# Revit family: Specialty_Equipment-Fiberglass_Planter-Planters_Unlimited-Baxter-Tapered Rectangular & Square-rev
name_source: partatom
category: Specialty Equipment
units: mm (PartAtom-declared; Revit-internal decimal feet)

## family parameters
Always vertical = Yes
Cut with Voids When Loaded = No
Enable Cutting in Views = No
Maintain Annotation Orientation = No
OmniClass Number = 23.40.05.21.17
OmniClass Title = Planters
Part Type = Normal
Room Calculation Point = No
Round Connector Dimension = Use Diameter
Shared = No
Work Plane-Based = No

## types (504) — shared parameters
Assembly Code = G2050600
CD_Finish = Plastic-Fiberglass-Carlsbad-Gloss-Black_Fox
CD_Microsite = https://www.caddetails.com
CD_Pad Size = 3"
CD_Pad Spacing = 5"
CD_Planter Lip = 1"
CD_Product Page URL = https://www.plantersunlimited.com
CD_Radius Baseplate = 6"
Default Elevation = 0"
Manufacturer = Planters Unlimited
Model = Baxter Tapered Series Planters
URL = https://www.plantersunlimited.com

## per-type parameters (varying)
| type | CD_Height | CD_Length | CD_Specification | CD_Width | Description | Type Comments |
| 30"L x 15"W x 18"H | 18" | 30" | https://www.plantersunlimited.com | 15" | Baxter Tapered Rectangular Planter | Tapered Rectangular Planter |
| 30"L x 15"W x 24"H | 24" | 30" | https://www.plantersunlimited.com | 15" | Baxter Tapered Rectangular Planter | Tapered Rectangular Planter |
| 30"L x 15"W x 30"H | 30" | 30" | https://www.plantersunlimited.com | 15" | Baxter Tapered Rectangular Planter | Tapered Rectangular Planter |
| 30"L x 15"W x 36"H | 36" | 30" | https://www.plantersunlimited.com | 15" | Baxter Tapered Rectangular Planter | Tapered Rectangular Planter |
| 30"L x 15"W x 42"H | 42" | 30" | https://www.plantersunlimited.com | 15" | Baxter Tapered Rectangular Planter | Tapered Rectangular Planter |
| 30"L x 15"W x 48"H | 48" | 30" | https://www.plantersunlimited.com | 15" | Baxter Tapered Rectangular Planter | Tapered Rectangular Planter |
| 30"L x 18"W x 18"H | 18" | 30" | https://www.plantersunlimited.com | 18" | Baxter Tapered Rectangular Planter | Tapered Rectangular Planter |
| 30"L x 18"W x 24"H | 24" | 30" | https://www.plantersunlimited.com | 18" | Baxter Tapered Rectangular Planter | Tapered Rectangular Planter |
| 30"L x 18"W x 30"H | 30" | 30" | https://www.plantersunlimited.com | 18" | Baxter Tapered Rectangular Planter | Tapered Rectangular Planter |
| 30"L x 18"W x 36"H | 36" | 30" | https://www.plantersunlimited.com | 18" | Baxter Tapered Rectangular Planter | Tapered Rectangular Planter |
| 30"L x 18"W x 42"H | 42" | 30" | https://www.plantersunlimited.com | 18" | Baxter Tapered Rectangular Planter | Tapered Rectangular Planter |
| 30"L x 18"W x 48"H | 48" | 30" | https://www.plantersunlimited.com | 18" | Baxter Tapered Rectangular Planter | Tapered Rectangular Planter |
| 30"L x 24"W x 18"H | 18" | 30" | https://www.plantersunlimited.com | 24" | Baxter Tapered Rectangular Planter | Tapered Rectangular Planter |
| 30"L x 24"W x 24"H | 24" | 30" | https://www.plantersunlimited.com | 24" | Baxter Tapered Rectangular Planter | Tapered Rectangular Planter |
| 30"L x 24"W x 30"H | 30" | 30" | https://www.plantersunlimited.com | 24" | Baxter Tapered Rectangular Planter | Tapered Rectangular Planter |
| 30"L x 24"W x 36"H | 36" | 30" | https://www.plantersunlimited.com | 24" | Baxter Tapered Rectangular Planter | Tapered Rectangular Planter |
| 30"L x 24"W x 42"H | 42" | 30" | https://www.plantersunlimited.com | 24" | Baxter Tapered Rectangular Planter | Tapered Rectangular Planter |
| 30"L x 24"W x 48"H | 48" | 30" | https://www.plantersunlimited.com | 24" | Baxter Tapered Rectangular Planter | Tapered Rectangular Planter |
| 30"L x 30"W x 18"H | 18" | 30" | https://www.plantersunlimited.com | 30" | Baxter Tapered Square Planter | Tapered Square Planter |
| 30"L x 30"W x 24"H | 24" | 30" | https://www.plantersunlimited.com | 30" | Baxter Tapered Square Planter | Tapered Square Planter |
| 30"L x 30"W x 30"H | 30" | 30" | https://www.plantersunlimited.com | 30" | Baxter Tapered Square Planter | Tapered Square Planter |
| 30"L x 30"W x 36"H | 36" | 30" |  | 30" | Baxter Tapered Square Planter | Tapered Square Planter |
| 30"L x 30"W x 42"H | 42" | 30" | https://www.plantersunlimited.com | 30" | Baxter Tapered Square Planter | Tapered Square Planter |
| 30"L x 30"W x 48"H | 48" | 30" | https://www.plantersunlimited.com | 30" | Baxter Tapered Square Planter | Tapered Square Planter |
| 30"L x 36"W x 18"H | 18" | 30" | https://www.plantersunlimited.com | 36" | Baxter Tapered Rectangular Planter | Tapered Rectangular Planter |
| 30"L x 36"W x 24"H | 24" | 30" | https://www.plantersunlimited.com | 36" | Baxter Tapered Rectangular Planter | Tapered Rectangular Planter |
| 30"L x 36"W x 30"H | 30" | 30" | https://www.plantersunlimited.com | 36" | Baxter Tapered Rectangular Planter | Tapered Rectangular Planter |
| 30"L x 36"W x 36"H | 36" | 30" | https://www.plantersunlimited.com | 36" | Baxter Tapered Rectangular Planter | Tapered Rectangular Planter |
| 30"L x 36"W x 42"H | 42" | 30" | https://www.plantersunlimited.com | 36" | Baxter Tapered Rectangular Planter | Tapered Rectangular Planter |
| 30"L x 36"W x 48"H | 48" | 30" | https://www.plantersunlimited.com | 36" | Baxter Tapered Rectangular Planter | Tapered Rectangular Planter |
| 30"L x 42"W x 18"H | 18" | 30" | https://www.plantersunlimited.com | 42" | Baxter Tapered Rectangular Planter | Tapered Rectangular Planter |
| 30"L x 42"W x 24"H | 24" | 30" | https://www.plantersunlimited.com | 42" | Baxter Tapered Rectangular Planter | Tapered Rectangular Planter |
| 30"L x 42"W x 30"H | 30" | 30" | https://www.plantersunlimited.com | 42" | Baxter Tapered Rectangular Planter | Tapered Rectangular Planter |
| 30"L x 42"W x 36"H | 36" | 30" | https://www.plantersunlimited.com | 42" | Baxter Tapered Rectangular Planter | Tapered Rectangular Planter |
| 30"L x 42"W x 42"H | 42" | 30" | https://www.plantersunlimited.com | 42" | Baxter Tapered Rectangular Planter | Tapered Rectangular Planter |
| 30"L x 42"W x 48"H | 48" | 30" | https://www.plantersunlimited.com | 42" | Baxter Tapered Rectangular Planter | Tapered Rectangular Planter |
| 36"L x 15"W x 18"H | 18" | 36" | https://www.plantersunlimited.com | 15" | Baxter Tapered Rectangular Planter | Tapered Rectangular Planter |
| 36"L x 15"W x 24"H | 24" | 36" | https://www.plantersunlimited.com | 15" | Baxter Tapered Rectangular Planter | Tapered Rectangular Planter |
| 36"L x 15"W x 30"H | 30" | 36" | https://www.plantersunlimited.com | 15" | Baxter Tapered Rectangular Planter | Tapered Rectangular Planter |
| 36"L x 15"W x 36"H | 36" | 36" | https://www.plantersunlimited.com | 15" | Baxter Tapered Rectangular Planter | Tapered Rectangular Planter |
| 36"L x 15"W x 42"H | 42" | 36" | https://www.plantersunlimited.com | 15" | Baxter Tapered Rectangular Planter | Tapered Rectangular Planter |
| 36"L x 15"W x 48"H | 48" | 36" | https://www.plantersunlimited.com | 15" | Baxter Tapered Rectangular Planter | Tapered Rectangular Planter |
| 36"L x 18"W x 18"H | 18" | 36" | https://www.plantersunlimited.com | 18" | Baxter Tapered Rectangular Planter | Tapered Rectangular Planter |
| 36"L x 18"W x 24"H | 24" | 36" | https://www.plantersunlimited.com | 18" | Baxter Tapered Rectangular Planter | Tapered Rectangular Planter |
| 36"L x 18"W x 30"H | 30" | 36" | https://www.plantersunlimited.com | 18" | Baxter Tapered Rectangular Planter | Tapered Rectangular Planter |
| 36"L x 18"W x 36"H | 36" | 36" | https://www.plantersunlimited.com | 18" | Baxter Tapered Rectangular Planter | Tapered Rectangular Planter |
| 36"L x 18"W x 42"H | 42" | 36" | https://www.plantersunlimited.com | 18" | Baxter Tapered Rectangular Planter | Tapered Rectangular Planter |
| 36"L x 18"W x 48"H | 48" | 36" | https://www.plantersunlimited.com | 18" | Baxter Tapered Rectangular Planter | Tapered Rectangular Planter |
| 36"L x 24"W x 18"H | 18" | 36" | https://www.plantersunlimited.com | 24" | Baxter Tapered Rectangular Planter | Tapered Rectangular Planter |
| 36"L x 24"W x 24"H | 24" | 36" | https://www.plantersunlimited.com | 24" | Baxter Tapered Rectangular Planter | Tapered Rectangular Planter |
| 36"L x 24"W x 30"H | 30" | 36" | https://www.plantersunlimited.com | 24" | Baxter Tapered Rectangular Planter | Tapered Rectangular Planter |
| 36"L x 24"W x 36"H | 36" | 36" | https://www.plantersunlimited.com | 24" | Baxter Tapered Rectangular Planter | Tapered Rectangular Planter |
| 36"L x 24"W x 42"H | 42" | 36" | https://www.plantersunlimited.com | 24" | Baxter Tapered Rectangular Planter | Tapered Rectangular Planter |
| 36"L x 24"W x 48"H | 48" | 36" | https://www.plantersunlimited.com | 24" | Baxter Tapered Rectangular Planter | Tapered Rectangular Planter |
| 36"L x 30"W x 18"H | 18" | 36" | https://www.plantersunlimited.com | 30" | Baxter Tapered Rectangular Planter | Tapered Rectangular Planter |
| 36"L x 30"W x 24"H | 24" | 36" | https://www.plantersunlimited.com | 30" | Baxter Tapered Rectangular Planter | Tapered Rectangular Planter |
| 36"L x 30"W x 30"H | 30" | 36" | https://www.plantersunlimited.com | 30" | Baxter Tapered Rectangular Planter | Tapered Rectangular Planter |
| 36"L x 30"W x 36"H | 36" | 36" | https://www.plantersunlimited.com | 30" | Baxter Tapered Rectangular Planter | Tapered Rectangular Planter |
| 36"L x 30"W x 42"H | 42" | 36" | https://www.plantersunlimited.com | 30" | Baxter Tapered Rectangular Planter | Tapered Rectangular Planter |
| 36"L x 30"W x 48"H | 48" | 36" | https://www.plantersunlimited.com | 30" | Baxter Tapered Rectangular Planter | Tapered Rectangular Planter |
| 36"L x 36"W x 18"H | 18" | 36" | https://www.plantersunlimited.com | 36" | Baxter Tapered Square Planter | Tapered Square Planter |
| 36"L x 36"W x 24"H | 24" | 36" | https://www.plantersunlimited.com | 36" | Baxter Tapered Square Planter | Tapered Square Planter |
| 36"L x 36"W x 30"H | 30" | 36" | https://www.plantersunlimited.com | 36" | Baxter Tapered Square Planter | Tapered Square Planter |
| 36"L x 36"W x 36"H | 36" | 36" | https://www.plantersunlimited.com | 36" | Baxter Tapered Square Planter | Tapered Square Planter |
| 36"L x 36"W x 42"H | 42" | 36" | https://www.plantersunlimited.com | 36" | Baxter Tapered Square Planter | Tapered Square Planter |
| 36"L x 36"W x 48"H | 48" | 36" | https://www.plantersunlimited.com | 36" | Baxter Tapered Square Planter | Tapered Square Planter |
| 36"L x 42"W x 18"H | 18" | 36" | https://www.plantersunlimited.com | 42" | Baxter Tapered Rectangular Planter | Tapered Rectangular Planter |
| 36"L x 42"W x 24"H | 24" | 36" | https://www.plantersunlimited.com | 42" | Baxter Tapered Rectangular Planter | Tapered Rectangular Planter |
| 36"L x 42"W x 30"H | 30" | 36" | https://www.plantersunlimited.com | 42" | Baxter Tapered Rectangular Planter | Tapered Rectangular Planter |
| 36"L x 42"W x 36"H | 36" | 36" | https://www.plantersunlimited.com | 42" | Baxter Tapered Rectangular Planter | Tapered Rectangular Planter |
| 36"L x 42"W x 42"H | 42" | 36" | https://www.plantersunlimited.com | 42" | Baxter Tapered Rectangular Planter | Tapered Rectangular Planter |
| 36"L x 42"W x 48"H | 48" | 36" | https://www.plantersunlimited.com | 42" | Baxter Tapered Rectangular Planter | Tapered Rectangular Planter |
| 42"L x 15"W x 18"H | 18" | 42" | https://www.plantersunlimited.com | 15" | Baxter Tapered Rectangular Planter | Tapered Rectangular Planter |
| 42"L x 15"W x 24"H | 24" | 42" | https://www.plantersunlimited.com | 15" | Baxter Tapered Rectangular Planter | Tapered Rectangular Planter |
| 42"L x 15"W x 30"H | 30" | 42" | https://www.plantersunlimited.com | 15" | Baxter Tapered Rectangular Planter | Tapered Rectangular Planter |
| 42"L x 15"W x 36"H | 36" | 42" | https://www.plantersunlimited.com | 15" | Baxter Tapered Rectangular Planter | Tapered Rectangular Planter |
| 42"L x 15"W x 42"H | 42" | 42" | https://www.plantersunlimited.com | 15" | Baxter Tapered Rectangular Planter | Tapered Rectangular Planter |
| 42"L x 15"W x 48"H | 48" | 42" | https://www.plantersunlimited.com | 15" | Baxter Tapered Rectangular Planter | Tapered Rectangular Planter |
| 42"L x 18"W x 18"H | 18" | 42" | https://www.plantersunlimited.com | 18" | Baxter Tapered Rectangular Planter | Tapered Rectangular Planter |
| 42"L x 18"W x 24"H | 24" | 42" | https://www.plantersunlimited.com | 18" | Baxter Tapered Rectangular Planter | Tapered Rectangular Planter |
| 42"L x 18"W x 30"H | 30" | 42" | https://www.plantersunlimited.com | 18" | Baxter Tapered Rectangular Planter | Tapered Rectangular Planter |
| 42"L x 18"W x 36"H | 36" | 42" | https://www.plantersunlimited.com | 18" | Baxter Tapered Rectangular Planter | Tapered Rectangular Planter |
| 42"L x 18"W x 42"H | 42" | 42" | https://www.plantersunlimited.com | 18" | Baxter Tapered Rectangular Planter | Tapered Rectangular Planter |
| 42"L x 18"W x 48"H | 48" | 42" | https://www.plantersunlimited.com | 18" | Baxter Tapered Rectangular Planter | Tapered Rectangular Planter |
| 42"L x 24"W x 18"H | 18" | 42" | https://www.plantersunlimited.com | 24" | Baxter Tapered Rectangular Planter | Tapered Rectangular Planter |
| 42"L x 24"W x 24"H | 24" | 42" | https://www.plantersunlimited.com | 24" | Baxter Tapered Rectangular Planter | Tapered Rectangular Planter |
| 42"L x 24"W x 30"H | 30" | 42" | https://www.plantersunlimited.com | 24" | Baxter Tapered Rectangular Planter | Tapered Rectangular Planter |
| 42"L x 24"W x 36"H | 36" | 42" | https://www.plantersunlimited.com | 24" | Baxter Tapered Rectangular Planter | Tapered Rectangular Planter |
| 42"L x 24"W x 42"H | 42" | 42" | https://www.plantersunlimited.com | 24" | Baxter Tapered Rectangular Planter | Tapered Rectangular Planter |
| 42"L x 24"W x 48"H | 48" | 42" | https://www.plantersunlimited.com | 24" | Baxter Tapered Rectangular Planter | Tapered Rectangular Planter |
| 42"L x 30"W x 18"H | 18" | 42" | https://www.plantersunlimited.com | 30" | Baxter Tapered Rectangular Planter | Tapered Rectangular Planter |
| 42"L x 30"W x 24"H | 24" | 42" | https://www.plantersunlimited.com | 30" | Baxter Tapered Rectangular Planter | Tapered Rectangular Planter |
| 42"L x 30"W x 30"H | 30" | 42" | https://www.plantersunlimited.com | 30" | Baxter Tapered Rectangular Planter | Tapered Rectangular Planter |
| 42"L x 30"W x 36"H | 36" | 42" | https://www.plantersunlimited.com | 30" | Baxter Tapered Rectangular Planter | Tapered Rectangular Planter |
| 42"L x 30"W x 42"H | 42" | 42" | https://www.plantersunlimited.com | 30" | Baxter Tapered Rectangular Planter | Tapered Rectangular Planter |
| 42"L x 30"W x 48"H | 48" | 42" | https://www.plantersunlimited.com | 30" | Baxter Tapered Rectangular Planter | Tapered Rectangular Planter |
| 42"L x 36"W x 18"H | 18" | 42" | https://www.plantersunlimited.com | 36" | Baxter Tapered Rectangular Planter | Tapered Rectangular Planter |
| 42"L x 36"W x 24"H | 24" | 42" | https://www.plantersunlimited.com | 36" | Baxter Tapered Rectangular Planter | Tapered Rectangular Planter |
| 42"L x 36"W x 30"H | 30" | 42" | https://www.plantersunlimited.com | 36" | Baxter Tapered Rectangular Planter | Tapered Rectangular Planter |
| 42"L x 36"W x 36"H | 36" | 42" | https://www.plantersunlimited.com | 36" | Baxter Tapered Rectangular Planter | Tapered Rectangular Planter |
| 42"L x 36"W x 42"H | 42" | 42" | https://www.plantersunlimited.com | 36" | Baxter Tapered Rectangular Planter | Tapered Rectangular Planter |
| 42"L x 36"W x 48"H | 48" | 42" | https://www.plantersunlimited.com | 36" | Baxter Tapered Rectangular Planter | Tapered Rectangular Planter |
| 42"L x 42"W x 18"H | 18" | 42" | https://www.plantersunlimited.com | 42" | Baxter Tapered Square Planter | Tapered Square Planter |
| 42"L x 42"W x 24"H | 24" | 42" | https://www.plantersunlimited.com | 42" | Baxter Tapered Square Planter | Tapered Square Planter |
| 42"L x 42"W x 30"H | 30" | 42" | https://www.plantersunlimited.com | 42" | Baxter Tapered Square Planter | Tapered Square Planter |
| 42"L x 42"W x 36"H | 36" | 42" | https://www.plantersunlimited.com | 42" | Baxter Tapered Square Planter | Tapered Square Planter |
| 42"L x 42"W x 42"H | 42" | 42" | https://www.plantersunlimited.com | 42" | Baxter Tapered Square Planter | Tapered Square Planter |
| 42"L x 42"W x 48"H | 48" | 42" | https://www.plantersunlimited.com | 42" | Baxter Tapered Square Planter | Tapered Square Planter |
| 48"L x 15"W x 18"H | 18" | 48" | https://www.plantersunlimited.com | 15" | Baxter Tapered Rectangular Planter | Tapered Rectangular Planter |
| 48"L x 15"W x 24"H | 24" | 48" | https://www.plantersunlimited.com | 15" | Baxter Tapered Rectangular Planter | Tapered Rectangular Planter |
| 48"L x 15"W x 30"H | 30" | 48" | https://www.plantersunlimited.com | 15" | Baxter Tapered Rectangular Planter | Tapered Rectangular Planter |
| 48"L x 15"W x 36"H | 36" | 48" | https://www.plantersunlimited.com | 15" | Baxter Tapered Rectangular Planter | Tapered Rectangular Planter |
| 48"L x 15"W x 42"H | 42" | 48" | https://www.plantersunlimited.com | 15" | Baxter Tapered Rectangular Planter | Tapered Rectangular Planter |
| 48"L x 15"W x 48"H | 48" | 48" | https://www.plantersunlimited.com | 15" | Baxter Tapered Rectangular Planter | Tapered Rectangular Planter |
| 48"L x 18"W x 18"H | 18" | 48" | https://www.plantersunlimited.com | 18" | Baxter Tapered Rectangular Planter | Tapered Rectangular Planter |
| 48"L x 18"W x 24"H | 24" | 48" | https://www.plantersunlimited.com | 18" | Baxter Tapered Rectangular Planter | Tapered Rectangular Planter |
| 48"L x 18"W x 30"H | 30" | 48" | https://www.plantersunlimited.com | 18" | Baxter Tapered Rectangular Planter | Tapered Rectangular Planter |
| 48"L x 18"W x 36"H | 36" | 48" | https://www.plantersunlimited.com | 18" | Baxter Tapered Rectangular Planter | Tapered Rectangular Planter |
| 48"L x 18"W x 42"H | 42" | 48" | https://www.plantersunlimited.com | 18" | Baxter Tapered Rectangular Planter | Tapered Rectangular Planter |
| 48"L x 18"W x 48"H | 48" | 48" | https://www.plantersunlimited.com | 18" | Baxter Tapered Rectangular Planter | Tapered Rectangular Planter |
| 48"L x 24"W x 18"H | 18" | 48" | https://www.plantersunlimited.com | 24" | Baxter Tapered Rectangular Planter | Tapered Rectangular Planter |
| 48"L x 24"W x 24"H | 24" | 48" | https://www.plantersunlimited.com | 24" | Baxter Tapered Rectangular Planter | Tapered Rectangular Planter |
| 48"L x 24"W x 30"H | 30" | 48" | https://www.plantersunlimited.com | 24" | Baxter Tapered Rectangular Planter | Tapered Rectangular Planter |
| 48"L x 24"W x 36"H | 36" | 48" | https://www.plantersunlimited.com | 24" | Baxter Tapered Rectangular Planter | Tapered Rectangular Planter |
| 48"L x 24"W x 42"H | 42" | 48" | https://www.plantersunlimited.com | 24" | Baxter Tapered Rectangular Planter | Tapered Rectangular Planter |
| 48"L x 24"W x 48"H | 48" | 48" | https://www.plantersunlimited.com | 24" | Baxter Tapered Rectangular Planter | Tapered Rectangular Planter |
| 48"L x 30"W x 18"H | 18" | 48" | https://www.plantersunlimited.com | 30" | Baxter Tapered Rectangular Planter | Tapered Rectangular Planter |
| 48"L x 30"W x 24"H | 24" | 48" | https://www.plantersunlimited.com | 30" | Baxter Tapered Rectangular Planter | Tapered Rectangular Planter |
| 48"L x 30"W x 30"H | 30" | 48" | https://www.plantersunlimited.com | 30" | Baxter Tapered Rectangular Planter | Tapered Rectangular Planter |
| 48"L x 30"W x 36"H | 36" | 48" | https://www.plantersunlimited.com | 30" | Baxter Tapered Rectangular Planter | Tapered Rectangular Planter |
| 48"L x 30"W x 42"H | 42" | 48" | https://www.plantersunlimited.com | 30" | Baxter Tapered Rectangular Planter | Tapered Rectangular Planter |
| 48"L x 30"W x 48"H | 48" | 48" | https://www.plantersunlimited.com | 30" | Baxter Tapered Rectangular Planter | Tapered Rectangular Planter |
| 48"L x 36"W x 18"H | 18" | 48" | https://www.plantersunlimited.com | 36" | Baxter Tapered Rectangular Planter | Tapered Rectangular Planter |
| 48"L x 36"W x 24"H | 24" | 48" | https://www.plantersunlimited.com | 36" | Baxter Tapered Rectangular Planter | Tapered Rectangular Planter |
| 48"L x 36"W x 30"H | 30" | 48" | https://www.plantersunlimited.com | 36" | Baxter Tapered Rectangular Planter | Tapered Rectangular Planter |
| 48"L x 36"W x 36"H | 36" | 48" | https://www.plantersunlimited.com | 36" | Baxter Tapered Rectangular Planter | Tapered Rectangular Planter |
| 48"L x 36"W x 42"H | 42" | 48" | https://www.plantersunlimited.com | 36" | Baxter Tapered Rectangular Planter | Tapered Rectangular Planter |
| 48"L x 36"W x 48"H | 48" | 48" | https://www.plantersunlimited.com | 36" | Baxter Tapered Rectangular Planter | Tapered Rectangular Planter |
| 48"L x 42"W x 18"H | 18" | 48" | https://www.plantersunlimited.com | 42" | Baxter Tapered Rectangular Planter | Tapered Rectangular Planter |
| 48"L x 42"W x 24"H | 24" | 48" | https://www.plantersunlimited.com | 42" | Baxter Tapered Rectangular Planter | Tapered Rectangular Planter |
| 48"L x 42"W x 30"H | 30" | 48" | https://www.plantersunlimited.com | 42" | Baxter Tapered Rectangular Planter | Tapered Rectangular Planter |
| 48"L x 42"W x 36"H | 36" | 48" | https://www.plantersunlimited.com | 42" | Baxter Tapered Rectangular Planter | Tapered Rectangular Planter |
| 48"L x 42"W x 42"H | 42" | 48" | https://www.plantersunlimited.com | 42" | Baxter Tapered Rectangular Planter | Tapered Rectangular Planter |
| 48"L x 42"W x 48"H | 48" | 48" | https://www.plantersunlimited.com | 42" | Baxter Tapered Rectangular Planter | Tapered Rectangular Planter |
| 54"L x 15"W x 18"H | 18" | 54" | https://www.plantersunlimited.com | 15" | Baxter Tapered Rectangular Planter | Tapered Rectangular Planter |
| 54"L x 15"W x 24"H | 24" | 54" | https://www.plantersunlimited.com | 15" | Baxter Tapered Rectangular Planter | Tapered Rectangular Planter |
| 54"L x 15"W x 30"H | 30" | 54" | https://www.plantersunlimited.com | 15" | Baxter Tapered Rectangular Planter | Tapered Rectangular Planter |
| 54"L x 15"W x 36"H | 36" | 54" | https://www.plantersunlimited.com | 15" | Baxter Tapered Rectangular Planter | Tapered Rectangular Planter |
| 54"L x 15"W x 42"H | 42" | 54" | https://www.plantersunlimited.com | 15" | Baxter Tapered Rectangular Planter | Tapered Rectangular Planter |
| 54"L x 15"W x 48"H | 48" | 54" | https://www.plantersunlimited.com | 15" | Baxter Tapered Rectangular Planter | Tapered Rectangular Planter |
| 54"L x 18"W x 18"H | 18" | 54" | https://www.plantersunlimited.com | 18" | Baxter Tapered Rectangular Planter | Tapered Rectangular Planter |
| 54"L x 18"W x 24"H | 24" | 54" | https://www.plantersunlimited.com | 18" | Baxter Tapered Rectangular Planter | Tapered Rectangular Planter |
| 54"L x 18"W x 30"H | 30" | 54" | https://www.plantersunlimited.com | 18" | Baxter Tapered Rectangular Planter | Tapered Rectangular Planter |
| 54"L x 18"W x 36"H | 36" | 54" | https://www.plantersunlimited.com | 18" | Baxter Tapered Rectangular Planter | Tapered Rectangular Planter |
| 54"L x 18"W x 42"H | 42" | 54" | https://www.plantersunlimited.com | 18" | Baxter Tapered Rectangular Planter | Tapered Rectangular Planter |
| 54"L x 18"W x 48"H | 48" | 54" | https://www.plantersunlimited.com | 18" | Baxter Tapered Rectangular Planter | Tapered Rectangular Planter |
| 54"L x 24"W x 18"H | 18" | 54" | https://www.plantersunlimited.com | 24" | Baxter Tapered Rectangular Planter | Tapered Rectangular Planter |
| 54"L x 24"W x 24"H | 24" | 54" | https://www.plantersunlimited.com | 24" | Baxter Tapered Rectangular Planter | Tapered Rectangular Planter |
| 54"L x 24"W x 30"H | 30" | 54" | https://www.plantersunlimited.com | 24" | Baxter Tapered Rectangular Planter | Tapered Rectangular Planter |
| 54"L x 24"W x 36"H | 36" | 54" | https://www.plantersunlimited.com | 24" | Baxter Tapered Rectangular Planter | Tapered Rectangular Planter |
| 54"L x 24"W x 42"H | 42" | 54" | https://www.plantersunlimited.com | 24" | Baxter Tapered Rectangular Planter | Tapered Rectangular Planter |
| 54"L x 24"W x 48"H | 48" | 54" | https://www.plantersunlimited.com | 24" | Baxter Tapered Rectangular Planter | Tapered Rectangular Planter |
| 54"L x 30"W x 18"H | 18" | 54" | https://www.plantersunlimited.com | 30" | Baxter Tapered Rectangular Planter | Tapered Rectangular Planter |
| 54"L x 30"W x 24"H | 24" | 54" | https://www.plantersunlimited.com | 30" | Baxter Tapered Rectangular Planter | Tapered Rectangular Planter |
| 54"L x 30"W x 30"H | 30" | 54" | https://www.plantersunlimited.com | 30" | Baxter Tapered Rectangular Planter | Tapered Rectangular Planter |
| 54"L x 30"W x 36"H | 36" | 54" | https://www.plantersunlimited.com | 30" | Baxter Tapered Rectangular Planter | Tapered Rectangular Planter |
| 54"L x 30"W x 42"H | 42" | 54" | https://www.plantersunlimited.com | 30" | Baxter Tapered Rectangular Planter | Tapered Rectangular Planter |
| 54"L x 30"W x 48"H | 48" | 54" | https://www.plantersunlimited.com | 30" | Baxter Tapered Rectangular Planter | Tapered Rectangular Planter |
| 54"L x 36"W x 18"H | 18" | 54" | https://www.plantersunlimited.com | 36" | Baxter Tapered Rectangular Planter | Tapered Rectangular Planter |
| 54"L x 36"W x 24"H | 24" | 54" | https://www.plantersunlimited.com | 36" | Baxter Tapered Rectangular Planter | Tapered Rectangular Planter |
| 54"L x 36"W x 30"H | 30" | 54" | https://www.plantersunlimited.com | 36" | Baxter Tapered Rectangular Planter | Tapered Rectangular Planter |
| 54"L x 36"W x 36"H | 36" | 54" | https://www.plantersunlimited.com | 36" | Baxter Tapered Rectangular Planter | Tapered Rectangular Planter |
| 54"L x 36"W x 42"H | 42" | 54" | https://www.plantersunlimited.com | 36" | Baxter Tapered Rectangular Planter | Tapered Rectangular Planter |
| 54"L x 36"W x 48"H | 48" | 54" | https://www.plantersunlimited.com | 36" | Baxter Tapered Rectangular Planter | Tapered Rectangular Planter |
| 54"L x 42"W x 18"H | 18" | 54" | https://www.plantersunlimited.com | 42" | Baxter Tapered Rectangular Planter | Tapered Rectangular Planter |
| 54"L x 42"W x 24"H | 24" | 54" | https://www.plantersunlimited.com | 42" | Baxter Tapered Rectangular Planter | Tapered Rectangular Planter |
| 54"L x 42"W x 30"H | 30" | 54" | https://www.plantersunlimited.com | 42" | Baxter Tapered Rectangular Planter | Tapered Rectangular Planter |
| 54"L x 42"W x 36"H | 36" | 54" | https://www.plantersunlimited.com | 42" | Baxter Tapered Rectangular Planter | Tapered Rectangular Planter |
| 54"L x 42"W x 42"H | 42" | 54" | https://www.plantersunlimited.com | 42" | Baxter Tapered Rectangular Planter | Tapered Rectangular Planter |
| 54"L x 42"W x 48"H | 48" | 54" | https://www.plantersunlimited.com | 42" | Baxter Tapered Rectangular Planter | Tapered Rectangular Planter |
| 60"L x 15"W x 18"H | 18" | 60" | https://www.plantersunlimited.com | 15" | Baxter Tapered Rectangular Planter | Tapered Rectangular Planter |
| 60"L x 15"W x 24"H | 24" | 60" | https://www.plantersunlimited.com | 15" | Baxter Tapered Rectangular Planter | Tapered Rectangular Planter |
| 60"L x 15"W x 30"H | 30" | 60" | https://www.plantersunlimited.com | 15" | Baxter Tapered Rectangular Planter | Tapered Rectangular Planter |
| 60"L x 15"W x 36"H | 36" | 60" | https://www.plantersunlimited.com | 15" | Baxter Tapered Rectangular Planter | Tapered Rectangular Planter |
| 60"L x 15"W x 42"H | 42" | 60" | https://www.plantersunlimited.com | 15" | Baxter Tapered Rectangular Planter | Tapered Rectangular Planter |
| 60"L x 15"W x 48"H | 48" | 60" | https://www.plantersunlimited.com | 15" | Baxter Tapered Rectangular Planter | Tapered Rectangular Planter |
| 60"L x 18"W x 18"H | 18" | 60" | https://www.plantersunlimited.com | 18" | Baxter Tapered Rectangular Planter | Tapered Rectangular Planter |
| 60"L x 18"W x 24"H | 24" | 60" | https://www.plantersunlimited.com | 18" | Baxter Tapered Rectangular Planter | Tapered Rectangular Planter |
| 60"L x 18"W x 30"H | 30" | 60" | https://www.plantersunlimited.com | 18" | Baxter Tapered Rectangular Planter | Tapered Rectangular Planter |
| 60"L x 18"W x 36"H | 36" | 60" | https://www.plantersunlimited.com | 18" | Baxter Tapered Rectangular Planter | Tapered Rectangular Planter |
| 60"L x 18"W x 42"H | 42" | 60" | https://www.plantersunlimited.com | 18" | Baxter Tapered Rectangular Planter | Tapered Rectangular Planter |
| 60"L x 18"W x 48"H | 48" | 60" | https://www.plantersunlimited.com | 18" | Baxter Tapered Rectangular Planter | Tapered Rectangular Planter |
| 60"L x 24"W x 18"H | 18" | 60" | https://www.plantersunlimited.com | 24" | Baxter Tapered Rectangular Planter | Tapered Rectangular Planter |
| 60"L x 24"W x 24"H | 24" | 60" | https://www.plantersunlimited.com | 24" | Baxter Tapered Rectangular Planter | Tapered Rectangular Planter |
| 60"L x 24"W x 30"H | 30" | 60" | https://www.plantersunlimited.com | 24" | Baxter Tapered Rectangular Planter | Tapered Rectangular Planter |
| 60"L x 24"W x 36"H | 36" | 60" | https://www.plantersunlimited.com | 24" | Baxter Tapered Rectangular Planter | Tapered Rectangular Planter |
| 60"L x 24"W x 42"H | 42" | 60" | https://www.plantersunlimited.com | 24" | Baxter Tapered Rectangular Planter | Tapered Rectangular Planter |
| 60"L x 24"W x 48"H | 48" | 60" | https://www.plantersunlimited.com | 24" | Baxter Tapered Rectangular Planter | Tapered Rectangular Planter |
| 60"L x 30"W x 18"H | 18" | 60" | https://www.plantersunlimited.com | 30" | Baxter Tapered Rectangular Planter | Tapered Rectangular Planter |
| 60"L x 30"W x 24"H | 24" | 60" | https://www.plantersunlimited.com | 30" | Baxter Tapered Rectangular Planter | Tapered Rectangular Planter |
| 60"L x 30"W x 30"H | 30" | 60" | https://www.plantersunlimited.com | 30" | Baxter Tapered Rectangular Planter | Tapered Rectangular Planter |
| 60"L x 30"W x 36"H | 36" | 60" | https://www.plantersunlimited.com | 30" | Baxter Tapered Rectangular Planter | Tapered Rectangular Planter |
| 60"L x 30"W x 42"H | 42" | 60" | https://www.plantersunlimited.com | 30" | Baxter Tapered Rectangular Planter | Tapered Rectangular Planter |
| 60"L x 30"W x 48"H | 48" | 60" | https://www.plantersunlimited.com | 30" | Baxter Tapered Rectangular Planter | Tapered Rectangular Planter |
| 60"L x 36"W x 18"H | 18" | 60" | https://www.plantersunlimited.com | 36" | Baxter Tapered Rectangular Planter | Tapered Rectangular Planter |
| 60"L x 36"W x 24"H | 24" | 60" | https://www.plantersunlimited.com | 36" | Baxter Tapered Rectangular Planter | Tapered Rectangular Planter |
| 60"L x 36"W x 30"H | 30" | 60" | https://www.plantersunlimited.com | 36" | Baxter Tapered Rectangular Planter | Tapered Rectangular Planter |
| 60"L x 36"W x 36"H | 36" | 60" | https://www.plantersunlimited.com | 36" | Baxter Tapered Rectangular Planter | Tapered Rectangular Planter |
| 60"L x 36"W x 42"H | 42" | 60" | https://www.plantersunlimited.com | 36" | Baxter Tapered Rectangular Planter | Tapered Rectangular Planter |
| 60"L x 36"W x 48"H | 48" | 60" | https://www.plantersunlimited.com | 36" | Baxter Tapered Rectangular Planter | Tapered Rectangular Planter |
| 60"L x 42"W x 18"H | 18" | 60" | https://www.plantersunlimited.com | 42" | Baxter Tapered Rectangular Planter | Tapered Rectangular Planter |
| 60"L x 42"W x 24"H | 24" | 60" | https://www.plantersunlimited.com | 42" | Baxter Tapered Rectangular Planter | Tapered Rectangular Planter |
| 60"L x 42"W x 30"H | 30" | 60" | https://www.plantersunlimited.com | 42" | Baxter Tapered Rectangular Planter | Tapered Rectangular Planter |
| 60"L x 42"W x 36"H | 36" | 60" | https://www.plantersunlimited.com | 42" | Baxter Tapered Rectangular Planter | Tapered Rectangular Planter |
| 60"L x 42"W x 42"H | 42" | 60" | https://www.plantersunlimited.com | 42" | Baxter Tapered Rectangular Planter | Tapered Rectangular Planter |
| 60"L x 42"W x 48"H | 48" | 60" | https://www.plantersunlimited.com | 42" | Baxter Tapered Rectangular Planter | Tapered Rectangular Planter |
| 66"L x 15"W x 18"H | 18" | 66" | https://www.plantersunlimited.com | 15" | Baxter Tapered Rectangular Planter | Tapered Rectangular Planter |
| 66"L x 15"W x 24"H | 24" | 66" | https://www.plantersunlimited.com | 15" | Baxter Tapered Rectangular Planter | Tapered Rectangular Planter |
| 66"L x 15"W x 30"H | 30" | 66" | https://www.plantersunlimited.com | 15" | Baxter Tapered Rectangular Planter | Tapered Rectangular Planter |
| 66"L x 15"W x 36"H | 36" | 66" | https://www.plantersunlimited.com | 15" | Baxter Tapered Rectangular Planter | Tapered Rectangular Planter |
| 66"L x 15"W x 42"H | 42" | 66" | https://www.plantersunlimited.com | 15" | Baxter Tapered Rectangular Planter | Tapered Rectangular Planter |
| 66"L x 15"W x 48"H | 48" | 66" | https://www.plantersunlimited.com | 15" | Baxter Tapered Rectangular Planter | Tapered Rectangular Planter |
| 66"L x 18"W x 18"H | 18" | 66" | https://www.plantersunlimited.com | 18" | Baxter Tapered Rectangular Planter | Tapered Rectangular Planter |
| 66"L x 18"W x 24"H | 24" | 66" | https://www.plantersunlimited.com | 18" | Baxter Tapered Rectangular Planter | Tapered Rectangular Planter |
| 66"L x 18"W x 30"H | 30" | 66" | https://www.plantersunlimited.com | 18" | Baxter Tapered Rectangular Planter | Tapered Rectangular Planter |
| 66"L x 18"W x 36"H | 36" | 66" | https://www.plantersunlimited.com | 18" | Baxter Tapered Rectangular Planter | Tapered Rectangular Planter |
| 66"L x 18"W x 42"H | 42" | 66" | https://www.plantersunlimited.com | 18" | Baxter Tapered Rectangular Planter | Tapered Rectangular Planter |
| 66"L x 18"W x 48"H | 48" | 66" | https://www.plantersunlimited.com | 18" | Baxter Tapered Rectangular Planter | Tapered Rectangular Planter |
| 66"L x 24"W x 18"H | 18" | 66" | https://www.plantersunlimited.com | 24" | Baxter Tapered Rectangular Planter | Tapered Rectangular Planter |
| 66"L x 24"W x 24"H | 24" | 66" | https://www.plantersunlimited.com | 24" | Baxter Tapered Rectangular Planter | Tapered Rectangular Planter |
| 66"L x 24"W x 30"H | 30" | 66" | https://www.plantersunlimited.com | 24" | Baxter Tapered Rectangular Planter | Tapered Rectangular Planter |
| 66"L x 24"W x 36"H | 36" | 66" | https://www.plantersunlimited.com | 24" | Baxter Tapered Rectangular Planter | Tapered Rectangular Planter |
| 66"L x 24"W x 42"H | 42" | 66" | https://www.plantersunlimited.com | 24" | Baxter Tapered Rectangular Planter | Tapered Rectangular Planter |
| 66"L x 24"W x 48"H | 48" | 66" | https://www.plantersunlimited.com | 24" | Baxter Tapered Rectangular Planter | Tapered Rectangular Planter |
| 66"L x 30"W x 18"H | 18" | 66" | https://www.plantersunlimited.com | 30" | Baxter Tapered Rectangular Planter | Tapered Rectangular Planter |
| 66"L x 30"W x 24"H | 24" | 66" | https://www.plantersunlimited.com | 30" | Baxter Tapered Rectangular Planter | Tapered Rectangular Planter |
| 66"L x 30"W x 30"H | 30" | 66" | https://www.plantersunlimited.com | 30" | Baxter Tapered Rectangular Planter | Tapered Rectangular Planter |
| 66"L x 30"W x 36"H | 36" | 66" | https://www.plantersunlimited.com | 30" | Baxter Tapered Rectangular Planter | Tapered Rectangular Planter |
| 66"L x 30"W x 42"H | 42" | 66" | https://www.plantersunlimited.com | 30" | Baxter Tapered Rectangular Planter | Tapered Rectangular Planter |
| 66"L x 30"W x 48"H | 48" | 66" | https://www.plantersunlimited.com | 30" | Baxter Tapered Rectangular Planter | Tapered Rectangular Planter |
| 66"L x 36"W x 18"H | 18" | 66" | https://www.plantersunlimited.com | 36" | Baxter Tapered Rectangular Planter | Tapered Rectangular Planter |
| 66"L x 36"W x 24"H | 24" | 66" | https://www.plantersunlimited.com | 36" | Baxter Tapered Rectangular Planter | Tapered Rectangular Planter |
| 66"L x 36"W x 30"H | 30" | 66" | https://www.plantersunlimited.com | 36" | Baxter Tapered Rectangular Planter | Tapered Rectangular Planter |
| 66"L x 36"W x 36"H | 36" | 66" | https://www.plantersunlimited.com | 36" | Baxter Tapered Rectangular Planter | Tapered Rectangular Planter |
| 66"L x 36"W x 42"H | 42" | 66" | https://www.plantersunlimited.com | 36" | Baxter Tapered Rectangular Planter | Tapered Rectangular Planter |
| 66"L x 36"W x 48"H | 48" | 66" | https://www.plantersunlimited.com | 36" | Baxter Tapered Rectangular Planter | Tapered Rectangular Planter |
| 66"L x 42"W x 18"H | 18" | 66" | https://www.plantersunlimited.com | 42" | Baxter Tapered Rectangular Planter | Tapered Rectangular Planter |
| 66"L x 42"W x 24"H | 24" | 66" | https://www.plantersunlimited.com | 42" | Baxter Tapered Rectangular Planter | Tapered Rectangular Planter |
| 66"L x 42"W x 30"H | 30" | 66" | https://www.plantersunlimited.com | 42" | Baxter Tapered Rectangular Planter | Tapered Rectangular Planter |
| 66"L x 42"W x 36"H | 36" | 66" | https://www.plantersunlimited.com | 42" | Baxter Tapered Rectangular Planter | Tapered Rectangular Planter |
| 66"L x 42"W x 42"H | 42" | 66" | https://www.plantersunlimited.com | 42" | Baxter Tapered Rectangular Planter | Tapered Rectangular Planter |
| 66"L x 42"W x 48"H | 48" | 66" | https://www.plantersunlimited.com | 42" | Baxter Tapered Rectangular Planter | Tapered Rectangular Planter |
| 72"L x 15"W x 18"H | 18" | 72" | https://www.plantersunlimited.com | 15" | Baxter Tapered Rectangular Planter | Tapered Rectangular Planter |
| 72"L x 15"W x 24"H | 24" | 72" | https://www.plantersunlimited.com | 15" | Baxter Tapered Rectangular Planter | Tapered Rectangular Planter |
| 72"L x 15"W x 30"H | 30" | 72" | https://www.plantersunlimited.com | 15" | Baxter Tapered Rectangular Planter | Tapered Rectangular Planter |
| 72"L x 15"W x 36"H | 36" | 72" | https://www.plantersunlimited.com | 15" | Baxter Tapered Rectangular Planter | Tapered Rectangular Planter |
| 72"L x 15"W x 42"H | 42" | 72" | https://www.plantersunlimited.com | 15" | Baxter Tapered Rectangular Planter | Tapered Rectangular Planter |
| 72"L x 15"W x 48"H | 48" | 72" | https://www.plantersunlimited.com | 15" | Baxter Tapered Rectangular Planter | Tapered Rectangular Planter |
| 72"L x 18"W x 18"H | 18" | 72" | https://www.plantersunlimited.com | 18" | Baxter Tapered Rectangular Planter | Tapered Rectangular Planter |
| 72"L x 18"W x 24"H | 24" | 72" | https://www.plantersunlimited.com | 18" | Baxter Tapered Rectangular Planter | Tapered Rectangular Planter |
| 72"L x 18"W x 30"H | 30" | 72" | https://www.plantersunlimited.com | 18" | Baxter Tapered Rectangular Planter | Tapered Rectangular Planter |
| 72"L x 18"W x 36"H | 36" | 72" | https://www.plantersunlimited.com | 18" | Baxter Tapered Rectangular Planter | Tapered Rectangular Planter |
| 72"L x 18"W x 42"H | 42" | 72" | https://www.plantersunlimited.com | 18" | Baxter Tapered Rectangular Planter | Tapered Rectangular Planter |
| 72"L x 18"W x 48"H | 48" | 72" | https://www.plantersunlimited.com | 18" | Baxter Tapered Rectangular Planter | Tapered Rectangular Planter |
| 72"L x 24"W x 18"H | 18" | 72" | https://www.plantersunlimited.com | 24" | Baxter Tapered Rectangular Planter | Tapered Rectangular Planter |
| 72"L x 24"W x 24"H | 24" | 72" | https://www.plantersunlimited.com | 24" | Baxter Tapered Rectangular Planter | Tapered Rectangular Planter |
| 72"L x 24"W x 30"H | 30" | 72" | https://www.plantersunlimited.com | 24" | Baxter Tapered Rectangular Planter | Tapered Rectangular Planter |
| 72"L x 24"W x 36"H | 36" | 72" | https://www.plantersunlimited.com | 24" | Baxter Tapered Rectangular Planter | Tapered Rectangular Planter |
| 72"L x 24"W x 42"H | 42" | 72" | https://www.plantersunlimited.com | 24" | Baxter Tapered Rectangular Planter | Tapered Rectangular Planter |
| 72"L x 24"W x 48"H | 48" | 72" | https://www.plantersunlimited.com | 24" | Baxter Tapered Rectangular Planter | Tapered Rectangular Planter |
| 72"L x 30"W x 18"H | 18" | 72" | https://www.plantersunlimited.com | 30" | Baxter Tapered Rectangular Planter | Tapered Rectangular Planter |
| 72"L x 30"W x 24"H | 24" | 72" | https://www.plantersunlimited.com | 30" | Baxter Tapered Rectangular Planter | Tapered Rectangular Planter |
| 72"L x 30"W x 30"H | 30" | 72" | https://www.plantersunlimited.com | 30" | Baxter Tapered Rectangular Planter | Tapered Rectangular Planter |
| 72"L x 30"W x 36"H | 36" | 72" | https://www.plantersunlimited.com | 30" | Baxter Tapered Rectangular Planter | Tapered Rectangular Planter |
| 72"L x 30"W x 42"H | 42" | 72" | https://www.plantersunlimited.com | 30" | Baxter Tapered Rectangular Planter | Tapered Rectangular Planter |
| 72"L x 30"W x 48"H | 48" | 72" | https://www.plantersunlimited.com | 30" | Baxter Tapered Rectangular Planter | Tapered Rectangular Planter |
| 72"L x 36"W x 18"H | 18" | 72" | https://www.plantersunlimited.com | 36" | Baxter Tapered Rectangular Planter | Tapered Rectangular Planter |
| 72"L x 36"W x 24"H | 24" | 72" | https://www.plantersunlimited.com | 36" | Baxter Tapered Rectangular Planter | Tapered Rectangular Planter |
| 72"L x 36"W x 30"H | 30" | 72" | https://www.plantersunlimited.com | 36" | Baxter Tapered Rectangular Planter | Tapered Rectangular Planter |
| 72"L x 36"W x 36"H | 36" | 72" | https://www.plantersunlimited.com | 36" | Baxter Tapered Rectangular Planter | Tapered Rectangular Planter |
| 72"L x 36"W x 42"H | 42" | 72" | https://www.plantersunlimited.com | 36" | Baxter Tapered Rectangular Planter | Tapered Rectangular Planter |
| 72"L x 36"W x 48"H | 48" | 72" | https://www.plantersunlimited.com | 36" | Baxter Tapered Rectangular Planter | Tapered Rectangular Planter |
| 72"L x 42"W x 18"H | 18" | 72" | https://www.plantersunlimited.com | 42" | Baxter Tapered Rectangular Planter | Tapered Rectangular Planter |
| 72"L x 42"W x 24"H | 24" | 72" | https://www.plantersunlimited.com | 42" | Baxter Tapered Rectangular Planter | Tapered Rectangular Planter |
| 72"L x 42"W x 30"H | 30" | 72" | https://www.plantersunlimited.com | 42" | Baxter Tapered Rectangular Planter | Tapered Rectangular Planter |
| 72"L x 42"W x 36"H | 36" | 72" | https://www.plantersunlimited.com | 42" | Baxter Tapered Rectangular Planter | Tapered Rectangular Planter |
| 72"L x 42"W x 42"H | 42" | 72" | https://www.plantersunlimited.com | 42" | Baxter Tapered Rectangular Planter | Tapered Rectangular Planter |
| 72"L x 42"W x 48"H | 48" | 72" | https://www.plantersunlimited.com | 42" | Baxter Tapered Rectangular Planter | Tapered Rectangular Planter |
| 78"L x 15"W x 18"H | 18" | 78" | https://www.plantersunlimited.com | 15" | Baxter Tapered Rectangular Planter | Tapered Rectangular Planter |
| 78"L x 15"W x 24"H | 24" | 78" | https://www.plantersunlimited.com | 15" | Baxter Tapered Rectangular Planter | Tapered Rectangular Planter |
| 78"L x 15"W x 30"H | 30" | 78" | https://www.plantersunlimited.com | 15" | Baxter Tapered Rectangular Planter | Tapered Rectangular Planter |
| 78"L x 15"W x 36"H | 36" | 78" | https://www.plantersunlimited.com | 15" | Baxter Tapered Rectangular Planter | Tapered Rectangular Planter |
| 78"L x 15"W x 42"H | 42" | 78" | https://www.plantersunlimited.com | 15" | Baxter Tapered Rectangular Planter | Tapered Rectangular Planter |
| 78"L x 15"W x 48"H | 48" | 78" | https://www.plantersunlimited.com | 15" | Baxter Tapered Rectangular Planter | Tapered Rectangular Planter |
| 78"L x 18"W x 18"H | 18" | 78" | https://www.plantersunlimited.com | 18" | Baxter Tapered Rectangular Planter | Tapered Rectangular Planter |
| 78"L x 18"W x 24"H | 24" | 78" | https://www.plantersunlimited.com | 18" | Baxter Tapered Rectangular Planter | Tapered Rectangular Planter |
| 78"L x 18"W x 30"H | 30" | 78" | https://www.plantersunlimited.com | 18" | Baxter Tapered Rectangular Planter | Tapered Rectangular Planter |
| 78"L x 18"W x 36"H | 36" | 78" | https://www.plantersunlimited.com | 18" | Baxter Tapered Rectangular Planter | Tapered Rectangular Planter |
| 78"L x 18"W x 42"H | 42" | 78" | https://www.plantersunlimited.com | 18" | Baxter Tapered Rectangular Planter | Tapered Rectangular Planter |
| 78"L x 18"W x 48"H | 48" | 78" | https://www.plantersunlimited.com | 18" | Baxter Tapered Rectangular Planter | Tapered Rectangular Planter |
| 78"L x 24"W x 18"H | 18" | 78" | https://www.plantersunlimited.com | 24" | Baxter Tapered Rectangular Planter | Tapered Rectangular Planter |
| 78"L x 24"W x 24"H | 24" | 78" | https://www.plantersunlimited.com | 24" | Baxter Tapered Rectangular Planter | Tapered Rectangular Planter |
| 78"L x 24"W x 30"H | 30" | 78" | https://www.plantersunlimited.com | 24" | Baxter Tapered Rectangular Planter | Tapered Rectangular Planter |
| 78"L x 24"W x 36"H | 36" | 78" | https://www.plantersunlimited.com | 24" | Baxter Tapered Rectangular Planter | Tapered Rectangular Planter |
| 78"L x 24"W x 42"H | 42" | 78" | https://www.plantersunlimited.com | 24" | Baxter Tapered Rectangular Planter | Tapered Rectangular Planter |
| 78"L x 24"W x 48"H | 48" | 78" | https://www.plantersunlimited.com | 24" | Baxter Tapered Rectangular Planter | Tapered Rectangular Planter |
| 78"L x 30"W x 18"H | 18" | 78" | https://www.plantersunlimited.com | 30" | Baxter Tapered Rectangular Planter | Tapered Rectangular Planter |
| 78"L x 30"W x 24"H | 24" | 78" | https://www.plantersunlimited.com | 30" | Baxter Tapered Rectangular Planter | Tapered Rectangular Planter |
| 78"L x 30"W x 30"H | 30" | 78" | https://www.plantersunlimited.com | 30" | Baxter Tapered Rectangular Planter | Tapered Rectangular Planter |
| 78"L x 30"W x 36"H | 36" | 78" | https://www.plantersunlimited.com | 30" | Baxter Tapered Rectangular Planter | Tapered Rectangular Planter |
| 78"L x 30"W x 42"H | 42" | 78" | https://www.plantersunlimited.com | 30" | Baxter Tapered Rectangular Planter | Tapered Rectangular Planter |
| 78"L x 30"W x 48"H | 48" | 78" | https://www.plantersunlimited.com | 30" | Baxter Tapered Rectangular Planter | Tapered Rectangular Planter |
| 78"L x 36"W x 18"H | 18" | 78" | https://www.plantersunlimited.com | 36" | Baxter Tapered Rectangular Planter | Tapered Rectangular Planter |
| 78"L x 36"W x 24"H | 24" | 78" | https://www.plantersunlimited.com | 36" | Baxter Tapered Rectangular Planter | Tapered Rectangular Planter |
| 78"L x 36"W x 30"H | 30" | 78" | https://www.plantersunlimited.com | 36" | Baxter Tapered Rectangular Planter | Tapered Rectangular Planter |
| 78"L x 36"W x 36"H | 36" | 78" | https://www.plantersunlimited.com | 36" | Baxter Tapered Rectangular Planter | Tapered Rectangular Planter |
| 78"L x 36"W x 42"H | 42" | 78" | https://www.plantersunlimited.com | 36" | Baxter Tapered Rectangular Planter | Tapered Rectangular Planter |
| 78"L x 36"W x 48"H | 48" | 78" | https://www.plantersunlimited.com | 36" | Baxter Tapered Rectangular Planter | Tapered Rectangular Planter |
| 78"L x 42"W x 18"H | 18" | 78" | https://www.plantersunlimited.com | 42" | Baxter Tapered Rectangular Planter | Tapered Rectangular Planter |
| 78"L x 42"W x 24"H | 24" | 78" | https://www.plantersunlimited.com | 42" | Baxter Tapered Rectangular Planter | Tapered Rectangular Planter |
| 78"L x 42"W x 30"H | 30" | 78" | https://www.plantersunlimited.com | 42" | Baxter Tapered Rectangular Planter | Tapered Rectangular Planter |
| 78"L x 42"W x 36"H | 36" | 78" | https://www.plantersunlimited.com | 42" | Baxter Tapered Rectangular Planter | Tapered Rectangular Planter |
| 78"L x 42"W x 42"H | 42" | 78" | https://www.plantersunlimited.com | 42" | Baxter Tapered Rectangular Planter | Tapered Rectangular Planter |
| 78"L x 42"W x 48"H | 48" | 78" | https://www.plantersunlimited.com | 42" | Baxter Tapered Rectangular Planter | Tapered Rectangular Planter |
| 84"L x 15"W x 18"H | 18" | 84" | https://www.plantersunlimited.com | 15" | Baxter Tapered Rectangular Planter | Tapered Rectangular Planter |
| 84"L x 15"W x 24"H | 24" | 84" | https://www.plantersunlimited.com | 15" | Baxter Tapered Rectangular Planter | Tapered Rectangular Planter |
| 84"L x 15"W x 30"H | 30" | 84" | https://www.plantersunlimited.com | 15" | Baxter Tapered Rectangular Planter | Tapered Rectangular Planter |
| 84"L x 15"W x 36"H | 36" | 84" | https://www.plantersunlimited.com | 15" | Baxter Tapered Rectangular Planter | Tapered Rectangular Planter |
| 84"L x 15"W x 42"H | 42" | 84" | https://www.plantersunlimited.com | 15" | Baxter Tapered Rectangular Planter | Tapered Rectangular Planter |
| 84"L x 15"W x 48"H | 48" | 84" | https://www.plantersunlimited.com | 15" | Baxter Tapered Rectangular Planter | Tapered Rectangular Planter |
| 84"L x 18"W x 18"H | 18" | 84" | https://www.plantersunlimited.com | 18" | Baxter Tapered Rectangular Planter | Tapered Rectangular Planter |
| 84"L x 18"W x 24"H | 24" | 84" | https://www.plantersunlimited.com | 18" | Baxter Tapered Rectangular Planter | Tapered Rectangular Planter |
| 84"L x 18"W x 30"H | 30" | 84" | https://www.plantersunlimited.com | 18" | Baxter Tapered Rectangular Planter | Tapered Rectangular Planter |
| 84"L x 18"W x 36"H | 36" | 84" | https://www.plantersunlimited.com | 18" | Baxter Tapered Rectangular Planter | Tapered Rectangular Planter |
| 84"L x 18"W x 42"H | 42" | 84" | https://www.plantersunlimited.com | 18" | Baxter Tapered Rectangular Planter | Tapered Rectangular Planter |
| 84"L x 18"W x 48"H | 48" | 84" | https://www.plantersunlimited.com | 18" | Baxter Tapered Rectangular Planter | Tapered Rectangular Planter |
| 84"L x 24"W x 18"H | 18" | 84" | https://www.plantersunlimited.com | 24" | Baxter Tapered Rectangular Planter | Tapered Rectangular Planter |
| 84"L x 24"W x 24"H | 24" | 84" | https://www.plantersunlimited.com | 24" | Baxter Tapered Rectangular Planter | Tapered Rectangular Planter |
| 84"L x 24"W x 30"H | 30" | 84" | https://www.plantersunlimited.com | 24" | Baxter Tapered Rectangular Planter | Tapered Rectangular Planter |
| 84"L x 24"W x 36"H | 36" | 84" | https://www.plantersunlimited.com | 24" | Baxter Tapered Rectangular Planter | Tapered Rectangular Planter |
| 84"L x 24"W x 42"H | 42" | 84" | https://www.plantersunlimited.com | 24" | Baxter Tapered Rectangular Planter | Tapered Rectangular Planter |
| 84"L x 24"W x 48"H | 48" | 84" | https://www.plantersunlimited.com | 24" | Baxter Tapered Rectangular Planter | Tapered Rectangular Planter |
| 84"L x 30"W x 18"H | 18" | 84" | https://www.plantersunlimited.com | 30" | Baxter Tapered Rectangular Planter | Tapered Rectangular Planter |
| 84"L x 30"W x 24"H | 24" | 84" | https://www.plantersunlimited.com | 30" | Baxter Tapered Rectangular Planter | Tapered Rectangular Planter |
| 84"L x 30"W x 30"H | 30" | 84" | https://www.plantersunlimited.com | 30" | Baxter Tapered Rectangular Planter | Tapered Rectangular Planter |
| 84"L x 30"W x 36"H | 36" | 84" | https://www.plantersunlimited.com | 30" | Baxter Tapered Rectangular Planter | Tapered Rectangular Planter |
| 84"L x 30"W x 42"H | 42" | 84" | https://www.plantersunlimited.com | 30" | Baxter Tapered Rectangular Planter | Tapered Rectangular Planter |
| 84"L x 30"W x 48"H | 48" | 84" | https://www.plantersunlimited.com | 30" | Baxter Tapered Rectangular Planter | Tapered Rectangular Planter |
| 84"L x 36"W x 18"H | 18" | 84" | https://www.plantersunlimited.com | 36" | Baxter Tapered Rectangular Planter | Tapered Rectangular Planter |
| 84"L x 36"W x 24"H | 24" | 84" | https://www.plantersunlimited.com | 36" | Baxter Tapered Rectangular Planter | Tapered Rectangular Planter |
| 84"L x 36"W x 30"H | 30" | 84" | https://www.plantersunlimited.com | 36" | Baxter Tapered Rectangular Planter | Tapered Rectangular Planter |
| 84"L x 36"W x 36"H | 36" | 84" | https://www.plantersunlimited.com | 36" | Baxter Tapered Rectangular Planter | Tapered Rectangular Planter |
| 84"L x 36"W x 42"H | 42" | 84" | https://www.plantersunlimited.com | 36" | Baxter Tapered Rectangular Planter | Tapered Rectangular Planter |
| 84"L x 36"W x 48"H | 48" | 84" | https://www.plantersunlimited.com | 36" | Baxter Tapered Rectangular Planter | Tapered Rectangular Planter |
| 84"L x 42"W x 18"H | 18" | 84" | https://www.plantersunlimited.com | 42" | Baxter Tapered Rectangular Planter | Tapered Rectangular Planter |
| 84"L x 42"W x 24"H | 24" | 84" | https://www.plantersunlimited.com | 42" | Baxter Tapered Rectangular Planter | Tapered Rectangular Planter |
| 84"L x 42"W x 30"H | 30" | 84" | https://www.plantersunlimited.com | 42" | Baxter Tapered Rectangular Planter | Tapered Rectangular Planter |
| 84"L x 42"W x 36"H | 36" | 84" | https://www.plantersunlimited.com | 42" | Baxter Tapered Rectangular Planter | Tapered Rectangular Planter |
| 84"L x 42"W x 42"H | 42" | 84" | https://www.plantersunlimited.com | 42" | Baxter Tapered Rectangular Planter | Tapered Rectangular Planter |
| 84"L x 42"W x 48"H | 48" | 84" | https://www.plantersunlimited.com | 42" | Baxter Tapered Rectangular Planter | Tapered Rectangular Planter |
| 90"L x 15"W x 18"H | 18" | 90" | https://www.plantersunlimited.com | 15" | Baxter Tapered Rectangular Planter | Tapered Rectangular Planter |
| 90"L x 15"W x 24"H | 24" | 90" | https://www.plantersunlimited.com | 15" | Baxter Tapered Rectangular Planter | Tapered Rectangular Planter |
| 90"L x 15"W x 30"H | 30" | 90" | https://www.plantersunlimited.com | 15" | Baxter Tapered Rectangular Planter | Tapered Rectangular Planter |
| 90"L x 15"W x 36"H | 36" | 90" | https://www.plantersunlimited.com | 15" | Baxter Tapered Rectangular Planter | Tapered Rectangular Planter |
| 90"L x 15"W x 42"H | 42" | 90" | https://www.plantersunlimited.com | 15" | Baxter Tapered Rectangular Planter | Tapered Rectangular Planter |
| 90"L x 15"W x 48"H | 48" | 90" | https://www.plantersunlimited.com | 15" | Baxter Tapered Rectangular Planter | Tapered Rectangular Planter |
| 90"L x 18"W x 18"H | 18" | 90" | https://www.plantersunlimited.com | 18" | Baxter Tapered Rectangular Planter | Tapered Rectangular Planter |
| 90"L x 18"W x 24"H | 24" | 90" | https://www.plantersunlimited.com | 18" | Baxter Tapered Rectangular Planter | Tapered Rectangular Planter |
| 90"L x 18"W x 30"H | 30" | 90" | https://www.plantersunlimited.com | 18" | Baxter Tapered Rectangular Planter | Tapered Rectangular Planter |
| 90"L x 18"W x 36"H | 36" | 90" | https://www.plantersunlimited.com | 18" | Baxter Tapered Rectangular Planter | Tapered Rectangular Planter |
| 90"L x 18"W x 42"H | 42" | 90" | https://www.plantersunlimited.com | 18" | Baxter Tapered Rectangular Planter | Tapered Rectangular Planter |
| 90"L x 18"W x 48"H | 48" | 90" | https://www.plantersunlimited.com | 18" | Baxter Tapered Rectangular Planter | Tapered Rectangular Planter |
| 90"L x 24"W x 18"H | 18" | 90" | https://www.plantersunlimited.com | 24" | Baxter Tapered Rectangular Planter | Tapered Rectangular Planter |
| 90"L x 24"W x 24"H | 24" | 90" | https://www.plantersunlimited.com | 24" | Baxter Tapered Rectangular Planter | Tapered Rectangular Planter |
| 90"L x 24"W x 30"H | 30" | 90" | https://www.plantersunlimited.com | 24" | Baxter Tapered Rectangular Planter | Tapered Rectangular Planter |
| 90"L x 24"W x 36"H | 36" | 90" | https://www.plantersunlimited.com | 24" | Baxter Tapered Rectangular Planter | Tapered Rectangular Planter |
| 90"L x 24"W x 42"H | 42" | 90" | https://www.plantersunlimited.com | 24" | Baxter Tapered Rectangular Planter | Tapered Rectangular Planter |
| 90"L x 24"W x 48"H | 48" | 90" | https://www.plantersunlimited.com | 24" | Baxter Tapered Rectangular Planter | Tapered Rectangular Planter |
| 90"L x 30"W x 18"H | 18" | 90" | https://www.plantersunlimited.com | 30" | Baxter Tapered Rectangular Planter | Tapered Rectangular Planter |
| 90"L x 30"W x 24"H | 24" | 90" | https://www.plantersunlimited.com | 30" | Baxter Tapered Rectangular Planter | Tapered Rectangular Planter |
| 90"L x 30"W x 30"H | 30" | 90" | https://www.plantersunlimited.com | 30" | Baxter Tapered Rectangular Planter | Tapered Rectangular Planter |
| 90"L x 30"W x 36"H | 36" | 90" | https://www.plantersunlimited.com | 30" | Baxter Tapered Rectangular Planter | Tapered Rectangular Planter |
| 90"L x 30"W x 42"H | 42" | 90" | https://www.plantersunlimited.com | 30" | Baxter Tapered Rectangular Planter | Tapered Rectangular Planter |
| 90"L x 30"W x 48"H | 48" | 90" | https://www.plantersunlimited.com | 30" | Baxter Tapered Rectangular Planter | Tapered Rectangular Planter |
| 90"L x 36"W x 18"H | 18" | 90" | https://www.plantersunlimited.com | 36" | Baxter Tapered Rectangular Planter | Tapered Rectangular Planter |
| 90"L x 36"W x 24"H | 24" | 90" | https://www.plantersunlimited.com | 36" | Baxter Tapered Rectangular Planter | Tapered Rectangular Planter |
| 90"L x 36"W x 30"H | 30" | 90" | https://www.plantersunlimited.com | 36" | Baxter Tapered Rectangular Planter | Tapered Rectangular Planter |
| 90"L x 36"W x 36"H | 36" | 90" | https://www.plantersunlimited.com | 36" | Baxter Tapered Rectangular Planter | Tapered Rectangular Planter |
| 90"L x 36"W x 42"H | 42" | 90" | https://www.plantersunlimited.com | 36" | Baxter Tapered Rectangular Planter | Tapered Rectangular Planter |
| 90"L x 36"W x 48"H | 48" | 90" | https://www.plantersunlimited.com | 36" | Baxter Tapered Rectangular Planter | Tapered Rectangular Planter |
| 90"L x 42"W x 18"H | 18" | 90" | https://www.plantersunlimited.com | 42" | Baxter Tapered Rectangular Planter | Tapered Rectangular Planter |
| 90"L x 42"W x 24"H | 24" | 90" | https://www.plantersunlimited.com | 42" | Baxter Tapered Rectangular Planter | Tapered Rectangular Planter |
| 90"L x 42"W x 30"H | 30" | 90" | https://www.plantersunlimited.com | 42" | Baxter Tapered Rectangular Planter | Tapered Rectangular Planter |
| 90"L x 42"W x 36"H | 36" | 90" | https://www.plantersunlimited.com | 42" | Baxter Tapered Rectangular Planter | Tapered Rectangular Planter |
| 90"L x 42"W x 42"H | 42" | 90" | https://www.plantersunlimited.com | 42" | Baxter Tapered Rectangular Planter | Tapered Rectangular Planter |
| 90"L x 42"W x 48"H | 48" | 90" | https://www.plantersunlimited.com | 42" | Baxter Tapered Rectangular Planter | Tapered Rectangular Planter |
| 96"L x 15"W x 18"H | 18" | 96" | https://www.plantersunlimited.com | 15" | Baxter Tapered Rectangular Planter | Tapered Rectangular Planter |
| 96"L x 15"W x 24"H | 24" | 96" | https://www.plantersunlimited.com | 15" | Baxter Tapered Rectangular Planter | Tapered Rectangular Planter |
| 96"L x 15"W x 30"H | 30" | 96" | https://www.plantersunlimited.com | 15" | Baxter Tapered Rectangular Planter | Tapered Rectangular Planter |
| 96"L x 15"W x 36"H | 36" | 96" | https://www.plantersunlimited.com | 15" | Baxter Tapered Rectangular Planter | Tapered Rectangular Planter |
| 96"L x 15"W x 42"H | 42" | 96" | https://www.plantersunlimited.com | 15" | Baxter Tapered Rectangular Planter | Tapered Rectangular Planter |
| 96"L x 15"W x 48"H | 48" | 96" | https://www.plantersunlimited.com | 15" | Baxter Tapered Rectangular Planter | Tapered Rectangular Planter |
| 96"L x 18"W x 18"H | 18" | 96" | https://www.plantersunlimited.com | 18" | Baxter Tapered Rectangular Planter | Tapered Rectangular Planter |
| 96"L x 18"W x 24"H | 24" | 96" | https://www.plantersunlimited.com | 18" | Baxter Tapered Rectangular Planter | Tapered Rectangular Planter |
| 96"L x 18"W x 30"H | 30" | 96" | https://www.plantersunlimited.com | 18" | Baxter Tapered Rectangular Planter | Tapered Rectangular Planter |
| 96"L x 18"W x 36"H | 36" | 96" | https://www.plantersunlimited.com | 18" | Baxter Tapered Rectangular Planter | Tapered Rectangular Planter |
| 96"L x 18"W x 42"H | 42" | 96" | https://www.plantersunlimited.com | 18" | Baxter Tapered Rectangular Planter | Tapered Rectangular Planter |
| 96"L x 18"W x 48"H | 48" | 96" | https://www.plantersunlimited.com | 18" | Baxter Tapered Rectangular Planter | Tapered Rectangular Planter |
| 96"L x 24"W x 18"H | 18" | 96" | https://www.plantersunlimited.com | 24" | Baxter Tapered Rectangular Planter | Tapered Rectangular Planter |
| 96"L x 24"W x 24"H | 24" | 96" | https://www.plantersunlimited.com | 24" | Baxter Tapered Rectangular Planter | Tapered Rectangular Planter |
| 96"L x 24"W x 30"H | 30" | 96" | https://www.plantersunlimited.com | 24" | Baxter Tapered Rectangular Planter | Tapered Rectangular Planter |
| 96"L x 24"W x 36"H | 36" | 96" | https://www.plantersunlimited.com | 24" | Baxter Tapered Rectangular Planter | Tapered Rectangular Planter |
| 96"L x 24"W x 42"H | 42" | 96" | https://www.plantersunlimited.com | 24" | Baxter Tapered Rectangular Planter | Tapered Rectangular Planter |
| 96"L x 24"W x 48"H | 48" | 96" | https://www.plantersunlimited.com | 24" | Baxter Tapered Rectangular Planter | Tapered Rectangular Planter |
| 96"L x 30"W x 18"H | 18" | 96" | https://www.plantersunlimited.com | 30" | Baxter Tapered Rectangular Planter | Tapered Rectangular Planter |
| 96"L x 30"W x 24"H | 24" | 96" | https://www.plantersunlimited.com | 30" | Baxter Tapered Rectangular Planter | Tapered Rectangular Planter |
| 96"L x 30"W x 30"H | 30" | 96" | https://www.plantersunlimited.com | 30" | Baxter Tapered Rectangular Planter | Tapered Rectangular Planter |
| 96"L x 30"W x 36"H | 36" | 96" | https://www.plantersunlimited.com | 30" | Baxter Tapered Rectangular Planter | Tapered Rectangular Planter |
| 96"L x 30"W x 42"H | 42" | 96" | https://www.plantersunlimited.com | 30" | Baxter Tapered Rectangular Planter | Tapered Rectangular Planter |
| 96"L x 30"W x 48"H | 48" | 96" | https://www.plantersunlimited.com | 30" | Baxter Tapered Rectangular Planter | Tapered Rectangular Planter |
| 96"L x 36"W x 18"H | 18" | 96" | https://www.plantersunlimited.com | 36" | Baxter Tapered Rectangular Planter | Tapered Rectangular Planter |
| 96"L x 36"W x 24"H | 24" | 96" | https://www.plantersunlimited.com | 36" | Baxter Tapered Rectangular Planter | Tapered Rectangular Planter |
| 96"L x 36"W x 30"H | 30" | 96" | https://www.plantersunlimited.com | 36" | Baxter Tapered Rectangular Planter | Tapered Rectangular Planter |
| 96"L x 36"W x 36"H | 36" | 96" | https://www.plantersunlimited.com | 36" | Baxter Tapered Rectangular Planter | Tapered Rectangular Planter |
| 96"L x 36"W x 42"H | 42" | 96" | https://www.plantersunlimited.com | 36" | Baxter Tapered Rectangular Planter | Tapered Rectangular Planter |
| 96"L x 36"W x 48"H | 48" | 96" | https://www.plantersunlimited.com | 36" | Baxter Tapered Rectangular Planter | Tapered Rectangular Planter |
| 96"L x 42"W x 18"H | 18" | 96" | https://www.plantersunlimited.com | 42" | Baxter Tapered Rectangular Planter | Tapered Rectangular Planter |
| 96"L x 42"W x 24"H | 24" | 96" | https://www.plantersunlimited.com | 42" | Baxter Tapered Rectangular Planter | Tapered Rectangular Planter |
| 96"L x 42"W x 30"H | 30" | 96" | https://www.plantersunlimited.com | 42" | Baxter Tapered Rectangular Planter | Tapered Rectangular Planter |
| 96"L x 42"W x 36"H | 36" | 96" | https://www.plantersunlimited.com | 42" | Baxter Tapered Rectangular Planter | Tapered Rectangular Planter |
| 96"L x 42"W x 42"H | 42" | 96" | https://www.plantersunlimited.com | 42" | Baxter Tapered Rectangular Planter | Tapered Rectangular Planter |
| 96"L x 42"W x 48"H | 48" | 96" | https://www.plantersunlimited.com | 42" | Baxter Tapered Rectangular Planter | Tapered Rectangular Planter |
| 108"L x 15"W x 18"H | 18" | 108" | https://www.plantersunlimited.com | 15" | Baxter Tapered Rectangular Planter | Tapered Rectangular Planter |
| 108"L x 15"W x 24"H | 24" | 108" | https://www.plantersunlimited.com | 15" | Baxter Tapered Rectangular Planter | Tapered Rectangular Planter |
| 108"L x 15"W x 30"H | 30" | 108" | https://www.plantersunlimited.com | 15" | Baxter Tapered Rectangular Planter | Tapered Rectangular Planter |
| 108"L x 15"W x 36"H | 36" | 108" | https://www.plantersunlimited.com | 15" | Baxter Tapered Rectangular Planter | Tapered Rectangular Planter |
| 108"L x 15"W x 42"H | 42" | 108" | https://www.plantersunlimited.com | 15" | Baxter Tapered Rectangular Planter | Tapered Rectangular Planter |
| 108"L x 15"W x 48"H | 48" | 108" | https://www.plantersunlimited.com | 15" | Baxter Tapered Rectangular Planter | Tapered Rectangular Planter |
| 108"L x 18"W x 18"H | 18" | 108" | https://www.plantersunlimited.com | 18" | Baxter Tapered Rectangular Planter | Tapered Rectangular Planter |
| 108"L x 18"W x 24"H | 24" | 108" | https://www.plantersunlimited.com | 18" | Baxter Tapered Rectangular Planter | Tapered Rectangular Planter |
| 108"L x 18"W x 30"H | 30" | 108" | https://www.plantersunlimited.com | 18" | Baxter Tapered Rectangular Planter | Tapered Rectangular Planter |
| 108"L x 18"W x 36"H | 36" | 108" | https://www.plantersunlimited.com | 18" | Baxter Tapered Rectangular Planter | Tapered Rectangular Planter |
| 108"L x 18"W x 42"H | 42" | 108" | https://www.plantersunlimited.com | 18" | Baxter Tapered Rectangular Planter | Tapered Rectangular Planter |
| 108"L x 18"W x 48"H | 48" | 108" | https://www.plantersunlimited.com | 18" | Baxter Tapered Rectangular Planter | Tapered Rectangular Planter |
| 108"L x 24"W x 18"H | 18" | 108" | https://www.plantersunlimited.com | 24" | Baxter Tapered Rectangular Planter | Tapered Rectangular Planter |
| 108"L x 24"W x 24"H | 24" | 108" | https://www.plantersunlimited.com | 24" | Baxter Tapered Rectangular Planter | Tapered Rectangular Planter |
| 108"L x 24"W x 30"H | 30" | 108" | https://www.plantersunlimited.com | 24" | Baxter Tapered Rectangular Planter | Tapered Rectangular Planter |
| 108"L x 24"W x 36"H | 36" | 108" | https://www.plantersunlimited.com | 24" | Baxter Tapered Rectangular Planter | Tapered Rectangular Planter |
| 108"L x 24"W x 42"H | 42" | 108" | https://www.plantersunlimited.com | 24" | Baxter Tapered Rectangular Planter | Tapered Rectangular Planter |
| 108"L x 24"W x 48"H | 48" | 108" | https://www.plantersunlimited.com | 24" | Baxter Tapered Rectangular Planter | Tapered Rectangular Planter |
| 108"L x 30"W x 18"H | 18" | 108" | https://www.plantersunlimited.com | 30" | Baxter Tapered Rectangular Planter | Tapered Rectangular Planter |
| 108"L x 30"W x 24"H | 24" | 108" | https://www.plantersunlimited.com | 30" | Baxter Tapered Rectangular Planter | Tapered Rectangular Planter |
| 108"L x 30"W x 30"H | 30" | 108" | https://www.plantersunlimited.com | 30" | Baxter Tapered Rectangular Planter | Tapered Rectangular Planter |
| 108"L x 30"W x 36"H | 36" | 108" | https://www.plantersunlimited.com | 30" | Baxter Tapered Rectangular Planter | Tapered Rectangular Planter |
| 108"L x 30"W x 42"H | 42" | 108" | https://www.plantersunlimited.com | 30" | Baxter Tapered Rectangular Planter | Tapered Rectangular Planter |
| 108"L x 30"W x 48"H | 48" | 108" | https://www.plantersunlimited.com | 30" | Baxter Tapered Rectangular Planter | Tapered Rectangular Planter |
| 108"L x 36"W x 18"H | 18" | 108" | https://www.plantersunlimited.com | 36" | Baxter Tapered Rectangular Planter | Tapered Rectangular Planter |
| 108"L x 36"W x 24"H | 24" | 108" | https://www.plantersunlimited.com | 36" | Baxter Tapered Rectangular Planter | Tapered Rectangular Planter |
| 108"L x 36"W x 30"H | 30" | 108" | https://www.plantersunlimited.com | 36" | Baxter Tapered Rectangular Planter | Tapered Rectangular Planter |
| 108"L x 36"W x 36"H | 36" | 108" | https://www.plantersunlimited.com | 36" | Baxter Tapered Rectangular Planter | Tapered Rectangular Planter |
| 108"L x 36"W x 42"H | 42" | 108" | https://www.plantersunlimited.com | 36" | Baxter Tapered Rectangular Planter | Tapered Rectangular Planter |
| 108"L x 36"W x 48"H | 48" | 108" | https://www.plantersunlimited.com | 36" | Baxter Tapered Rectangular Planter | Tapered Rectangular Planter |
| 108"L x 42"W x 18"H | 18" | 108" | https://www.plantersunlimited.com | 42" | Baxter Tapered Rectangular Planter | Tapered Rectangular Planter |
| 108"L x 42"W x 24"H | 24" | 108" | https://www.plantersunlimited.com | 42" | Baxter Tapered Rectangular Planter | Tapered Rectangular Planter |
| 108"L x 42"W x 30"H | 30" | 108" | https://www.plantersunlimited.com | 42" | Baxter Tapered Rectangular Planter | Tapered Rectangular Planter |
| 108"L x 42"W x 36"H | 36" | 108" | https://www.plantersunlimited.com | 42" | Baxter Tapered Rectangular Planter | Tapered Rectangular Planter |
| 108"L x 42"W x 42"H | 42" | 108" | https://www.plantersunlimited.com | 42" | Baxter Tapered Rectangular Planter | Tapered Rectangular Planter |
| 108"L x 42"W x 48"H | 48" | 108" | https://www.plantersunlimited.com | 42" | Baxter Tapered Rectangular Planter | Tapered Rectangular Planter |
| 120"L x 15"W x 18"H | 18" | 120" | https://www.plantersunlimited.com | 15" | Baxter Tapered Rectangular Planter | Tapered Rectangular Planter |
| 120"L x 15"W x 24"H | 24" | 120" | https://www.plantersunlimited.com | 15" | Baxter Tapered Rectangular Planter | Tapered Rectangular Planter |
| 120"L x 15"W x 30"H | 30" | 120" | https://www.plantersunlimited.com | 15" | Baxter Tapered Rectangular Planter | Tapered Rectangular Planter |
| 120"L x 15"W x 36"H | 36" | 120" | https://www.plantersunlimited.com | 15" | Baxter Tapered Rectangular Planter | Tapered Rectangular Planter |
| 120"L x 15"W x 42"H | 42" | 120" | https://www.plantersunlimited.com | 15" | Baxter Tapered Rectangular Planter | Tapered Rectangular Planter |
| 120"L x 15"W x 48"H | 48" | 120" | https://www.plantersunlimited.com | 15" | Baxter Tapered Rectangular Planter | Tapered Rectangular Planter |
| 120"L x 18"W x 18"H | 18" | 120" | https://www.plantersunlimited.com | 18" | Baxter Tapered Rectangular Planter | Tapered Rectangular Planter |
| 120"L x 18"W x 24"H | 24" | 120" | https://www.plantersunlimited.com | 18" | Baxter Tapered Rectangular Planter | Tapered Rectangular Planter |
| 120"L x 18"W x 30"H | 30" | 120" | https://www.plantersunlimited.com | 18" | Baxter Tapered Rectangular Planter | Tapered Rectangular Planter |
| 120"L x 18"W x 36"H | 36" | 120" | https://www.plantersunlimited.com | 18" | Baxter Tapered Rectangular Planter | Tapered Rectangular Planter |
| 120"L x 18"W x 42"H | 42" | 120" | https://www.plantersunlimited.com | 18" | Baxter Tapered Rectangular Planter | Tapered Rectangular Planter |
| 120"L x 18"W x 48"H | 48" | 120" | https://www.plantersunlimited.com | 18" | Baxter Tapered Rectangular Planter | Tapered Rectangular Planter |
| 120"L x 24"W x 18"H | 18" | 120" | https://www.plantersunlimited.com | 24" | Baxter Tapered Rectangular Planter | Tapered Rectangular Planter |
| 120"L x 24"W x 24"H | 24" | 120" | https://www.plantersunlimited.com | 24" | Baxter Tapered Rectangular Planter | Tapered Rectangular Planter |
| 120"L x 24"W x 30"H | 30" | 120" | https://www.plantersunlimited.com | 24" | Baxter Tapered Rectangular Planter | Tapered Rectangular Planter |
| 120"L x 24"W x 36"H | 36" | 120" | https://www.plantersunlimited.com | 24" | Baxter Tapered Rectangular Planter | Tapered Rectangular Planter |
| 120"L x 24"W x 42"H | 42" | 120" | https://www.plantersunlimited.com | 24" | Baxter Tapered Rectangular Planter | Tapered Rectangular Planter |
| 120"L x 24"W x 48"H | 48" | 120" | https://www.plantersunlimited.com | 24" | Baxter Tapered Rectangular Planter | Tapered Rectangular Planter |
| 120"L x 30"W x 18"H | 18" | 120" | https://www.plantersunlimited.com | 30" | Baxter Tapered Rectangular Planter | Tapered Rectangular Planter |
| 120"L x 30"W x 24"H | 24" | 120" | https://www.plantersunlimited.com | 30" | Baxter Tapered Rectangular Planter | Tapered Rectangular Planter |
| 120"L x 30"W x 30"H | 30" | 120" | https://www.plantersunlimited.com | 30" | Baxter Tapered Rectangular Planter | Tapered Rectangular Planter |
| 120"L x 30"W x 36"H | 36" | 120" | https://www.plantersunlimited.com | 30" | Baxter Tapered Rectangular Planter | Tapered Rectangular Planter |
| 120"L x 30"W x 42"H | 42" | 120" | https://www.plantersunlimited.com | 30" | Baxter Tapered Rectangular Planter | Tapered Rectangular Planter |
| 120"L x 30"W x 48"H | 48" | 120" | https://www.plantersunlimited.com | 30" | Baxter Tapered Rectangular Planter | Tapered Rectangular Planter |
| 120"L x 36"W x 18"H | 18" | 120" | https://www.plantersunlimited.com | 36" | Baxter Tapered Rectangular Planter | Tapered Rectangular Planter |
| 120"L x 36"W x 24"H | 24" | 120" | https://www.plantersunlimited.com | 36" | Baxter Tapered Rectangular Planter | Tapered Rectangular Planter |
| 120"L x 36"W x 30"H | 30" | 120" | https://www.plantersunlimited.com | 36" | Baxter Tapered Rectangular Planter | Tapered Rectangular Planter |
| 120"L x 36"W x 36"H | 36" | 120" | https://www.plantersunlimited.com | 36" | Baxter Tapered Rectangular Planter | Tapered Rectangular Planter |
| 120"L x 36"W x 42"H | 42" | 120" | https://www.plantersunlimited.com | 36" | Baxter Tapered Rectangular Planter | Tapered Rectangular Planter |
| 120"L x 36"W x 48"H | 48" | 120" | https://www.plantersunlimited.com | 36" | Baxter Tapered Rectangular Planter | Tapered Rectangular Planter |
| 120"L x 42"W x 18"H | 18" | 120" | https://www.plantersunlimited.com | 42" | Baxter Tapered Rectangular Planter | Tapered Rectangular Planter |
| 120"L x 42"W x 24"H | 24" | 120" | https://www.plantersunlimited.com | 42" | Baxter Tapered Rectangular Planter | Tapered Rectangular Planter |
| 120"L x 42"W x 30"H | 30" | 120" | https://www.plantersunlimited.com | 42" | Baxter Tapered Rectangular Planter | Tapered Rectangular Planter |
| 120"L x 42"W x 36"H | 36" | 120" | https://www.plantersunlimited.com | 42" | Baxter Tapered Rectangular Planter | Tapered Rectangular Planter |
| 120"L x 42"W x 42"H | 42" | 120" | https://www.plantersunlimited.com | 42" | Baxter Tapered Rectangular Planter | Tapered Rectangular Planter |
| 120"L x 42"W x 48"H | 48" | 120" | https://www.plantersunlimited.com | 42" | Baxter Tapered Rectangular Planter | Tapered Rectangular Planter |

## geometry (parser evidence)
native form markers: Sweep x2
no freeform markers — native parametric forms only
